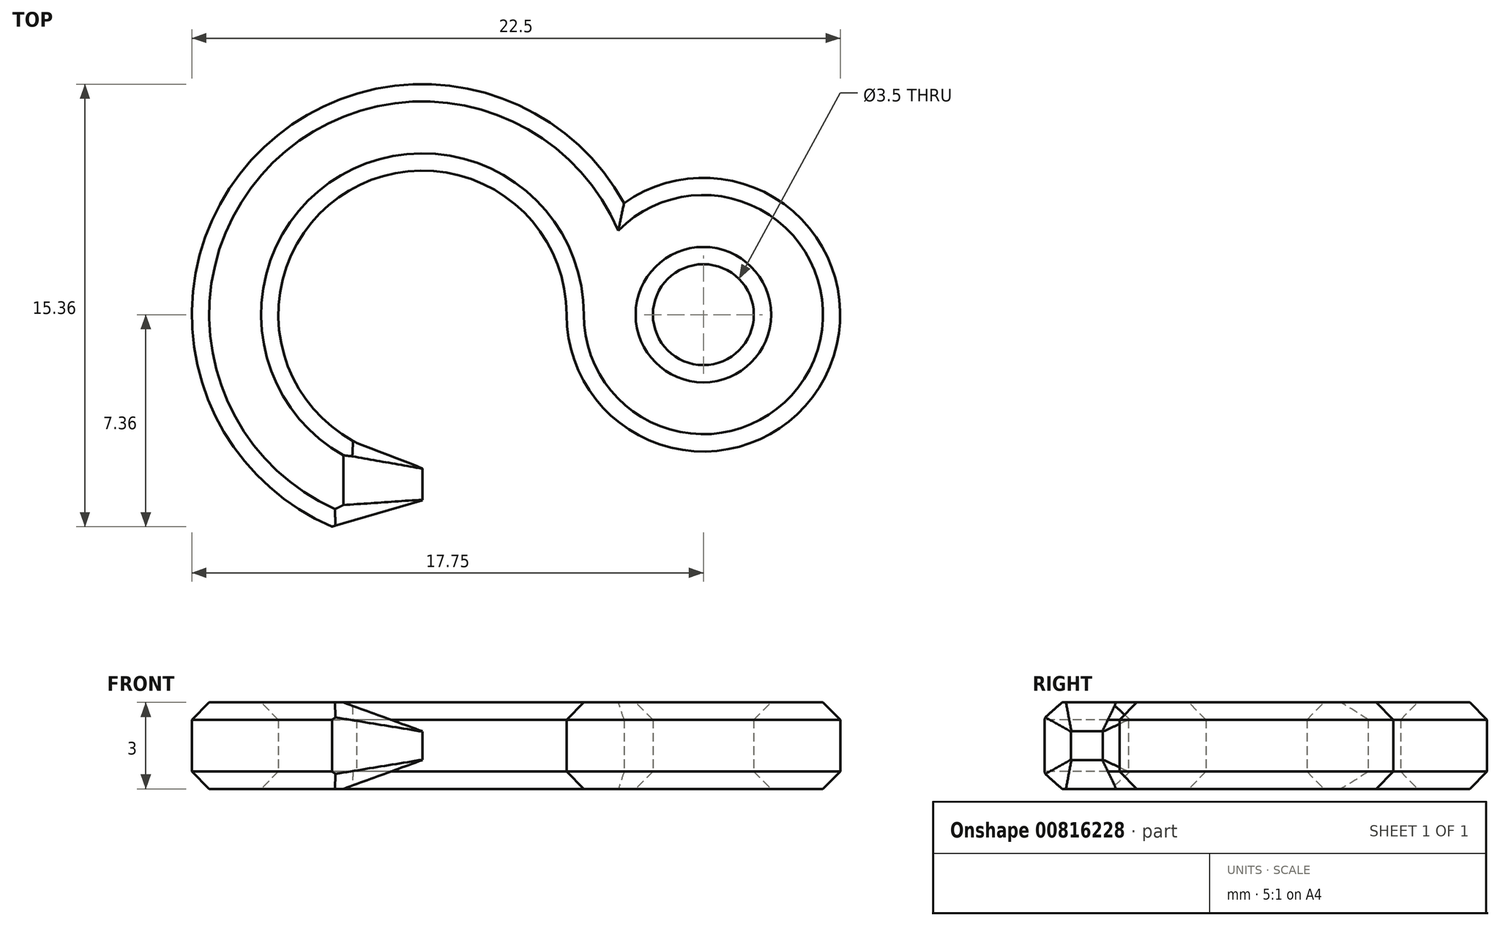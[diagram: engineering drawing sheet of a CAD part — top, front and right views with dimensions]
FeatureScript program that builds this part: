
annotation { "Feature Type Name" : "Feature", "Feature Type Description" : "" }
export const myFeature = defineFeature(function(context is Context, id is Id, definition is map)
    precondition{}
    {
        {
            var Q0;
            Q0=qCreatedBy(makeId("Top.planeOp"),FACE);
            var sketch = newSketch(context, id + "F0", { "sketchPlane" : qUnion([Q0])});
            skCircle(sketch, "E0", {"center": v(0, 0) * mm, "radius": 5 * mm});
            skCircle(sketch, "E1", {"center": v(9.75, 0) * mm, "radius": 1.75 * mm});
            skLineSegment(sketch, "E2", {"start": v(5, 0) * mm, "end": v(8, 0) * mm, "construction": true});
            skCircle(sketch, "E3.0", {"center": v(0, 0) * mm, "radius": 8 * mm});
            skCircle(sketch, "E4.0", {"center": v(9.75, 0) * mm, "radius": 4.75 * mm});
            skLineSegment(sketch, "E5", {"start": v(0, -5) * mm, "end": v(0, -8) * mm});
            skSolve(sketch);
        }
        {
            var Q0;
            {var subQ0=sQuery(id+"F0.wireOp",EDGE,"E5");Q0=makeQuery(id+"F0.imprint","IMPRINT",FACE,{"disambiguationData":[TD([[makeQuery(id+"F0.imprint","IMPRINT",EDGE,{"derivedFrom":subQ0}),-1.0]])]});}
            var Q1;
            {var subQ0=sQuery(id+"F0.wireOp",EDGE,"E3.0");var subQ1=makeQuery(id+"F0.imprint","INTERSECT",VERTEX,{"derivedFrom":[sQuery(id+"F0.wireOp",EDGE,"E1"),subQ0]});Q1=makeQuery(id+"F0.imprint","IMPRINT",FACE,{"disambiguationData":[TD([[makeQuery(id+"F0.imprint","IMPRINT",EDGE,{"disambiguationData":[TD([[subQ1,-1.0]])],"derivedFrom":subQ0}),1.0]])]});}
            var Q2;
            {var subQ0=sQuery(id+"F0.wireOp",EDGE,"E1");Q2=makeQuery(id+"F0.imprint","IMPRINT",FACE,{"disambiguationData":[TD([[makeQuery(id+"F0.imprint","IMPRINT",EDGE,{"derivedFrom":subQ0}),-1.0]])]});}
            extrude(context, id + "F1", {"entities" : qUnion([Q0, Q1, Q2]), "depth" : 3 * mm, "offsetDistance" : 25 * mm});
        }
        {
            var Q0;
            Q0=makeQuery(id+"F1.opExtrude","CAP_EDGE",EDGE,{"disambiguationData":[OSD([sQuery(id+"F0.wireOp",EDGE,"E0")])],"isStart":false});
            var Q1;
            Q1=makeQuery(id+"F1.opExtrude","CAP_EDGE",EDGE,{"disambiguationData":[OSD([sQuery(id+"F0.wireOp",EDGE,"E3.0")])],"isStart":false});
            var Q2;
            Q2=makeQuery(id+"F1.opExtrude","CAP_EDGE",EDGE,{"disambiguationData":[OSD([sQuery(id+"F0.wireOp",EDGE,"E4.0")])],"isStart":false});
            var Q3;
            Q3=makeQuery(id+"F1.opExtrude","CAP_EDGE",EDGE,{"disambiguationData":[OSD([sQuery(id+"F0.wireOp",EDGE,"E1")])],"isStart":false});
            var Q4;
            Q4=makeQuery(id+"F1.opExtrude","CAP_EDGE",EDGE,{"disambiguationData":[OSD([sQuery(id+"F0.wireOp",EDGE,"E4.0")])],"isStart":true});
            var Q5;
            Q5=makeQuery(id+"F1.opExtrude","CAP_EDGE",EDGE,{"disambiguationData":[OSD([sQuery(id+"F0.wireOp",EDGE,"E0")])],"isStart":true});
            var Q6;
            Q6=makeQuery(id+"F1.opExtrude","CAP_EDGE",EDGE,{"disambiguationData":[OSD([sQuery(id+"F0.wireOp",EDGE,"E3.0")])],"isStart":true});
            var Q7;
            Q7=makeQuery(id+"F1.opExtrude","CAP_EDGE",EDGE,{"disambiguationData":[OSD([sQuery(id+"F0.wireOp",EDGE,"E1")])],"isStart":true});
            chamfer(context, id + "F2", {"entities" : qUnion([Q0, Q1, Q2, Q3, Q4, Q5, Q6, Q7]), "width" : 0.6 * mm, "tangentPropagation" : true});
        }
        {
            var Q0;
            Q0=makeQuery(id+"F1.opExtrude","CAP_EDGE",EDGE,{"disambiguationData":[OSD([sQuery(id+"F0.wireOp",EDGE,"E5")])],"isStart":false});
            var Q1;
            Q1=makeQuery(id+"F1.opExtrude","CAP_EDGE",EDGE,{"disambiguationData":[OSD([sQuery(id+"F0.wireOp",EDGE,"E5")])],"isStart":true});
            var Q2;
            Q2=makeQuery(id+"F1.opExtrude","SWEPT_EDGE",EDGE,{"disambiguationData":[OSD([sQuery(id+"F0.wireOp",EDGE,"E0"),sQuery(id+"F0.wireOp",EDGE,"E5")])]});
            var Q3;
            Q3=makeQuery(id+"F1.opExtrude","SWEPT_EDGE",EDGE,{"disambiguationData":[OSD([sQuery(id+"F0.wireOp",EDGE,"E3.0"),sQuery(id+"F0.wireOp",EDGE,"E5")])]});
            var Q4;
            Q4=makeQuery(id+"F2.opChamfer","BLEND_EDGE",EDGE,{"blendedFrom":[makeQuery(id+"F1.opExtrude","CAP_EDGE",EDGE,{"disambiguationData":[OSD([sQuery(id+"F0.wireOp",EDGE,"E3.0")])],"isStart":false}),makeQuery(id+"F1.opExtrude","SWEPT_FACE",FACE,{"disambiguationData":[OSD([sQuery(id+"F0.wireOp",EDGE,"E5")])]})],"blendedInto":[makeQuery(id+"F1.opExtrude","SWEPT_FACE",FACE,{"disambiguationData":[OSD([sQuery(id+"F0.wireOp",EDGE,"E5")])]})]});
            var Q5;
            Q5=makeQuery(id+"F2.opChamfer","BLEND_EDGE",EDGE,{"blendedFrom":[makeQuery(id+"F1.opExtrude","CAP_EDGE",EDGE,{"disambiguationData":[OSD([sQuery(id+"F0.wireOp",EDGE,"E3.0")])],"isStart":true}),makeQuery(id+"F1.opExtrude","SWEPT_FACE",FACE,{"disambiguationData":[OSD([sQuery(id+"F0.wireOp",EDGE,"E5")])]})],"blendedInto":[makeQuery(id+"F1.opExtrude","SWEPT_FACE",FACE,{"disambiguationData":[OSD([sQuery(id+"F0.wireOp",EDGE,"E5")])]})]});
            var Q6;
            Q6=makeQuery(id+"F2.opChamfer","BLEND_EDGE",EDGE,{"blendedFrom":[makeQuery(id+"F1.opExtrude","CAP_EDGE",EDGE,{"disambiguationData":[OSD([sQuery(id+"F0.wireOp",EDGE,"E0")])],"isStart":true}),makeQuery(id+"F1.opExtrude","SWEPT_FACE",FACE,{"disambiguationData":[OSD([sQuery(id+"F0.wireOp",EDGE,"E5")])]})],"blendedInto":[makeQuery(id+"F1.opExtrude","SWEPT_FACE",FACE,{"disambiguationData":[OSD([sQuery(id+"F0.wireOp",EDGE,"E5")])]})]});
            var Q7;
            Q7=makeQuery(id+"F2.opChamfer","BLEND_EDGE",EDGE,{"blendedFrom":[makeQuery(id+"F1.opExtrude","CAP_EDGE",EDGE,{"disambiguationData":[OSD([sQuery(id+"F0.wireOp",EDGE,"E0")])],"isStart":false}),makeQuery(id+"F1.opExtrude","SWEPT_FACE",FACE,{"disambiguationData":[OSD([sQuery(id+"F0.wireOp",EDGE,"E5")])]})],"blendedInto":[makeQuery(id+"F1.opExtrude","SWEPT_FACE",FACE,{"disambiguationData":[OSD([sQuery(id+"F0.wireOp",EDGE,"E5")])]})]});
            chamfer(context, id + "F3", {"entities" : qUnion([Q0, Q1, Q2, Q3, Q4, Q5, Q6, Q7]), "chamferType" : ChamferType.OFFSET_ANGLE, "width" : 1 * mm, "oppositeDirection" : false, "angle" : 70 * degree, "tangentPropagation" : true});
        }
    });
